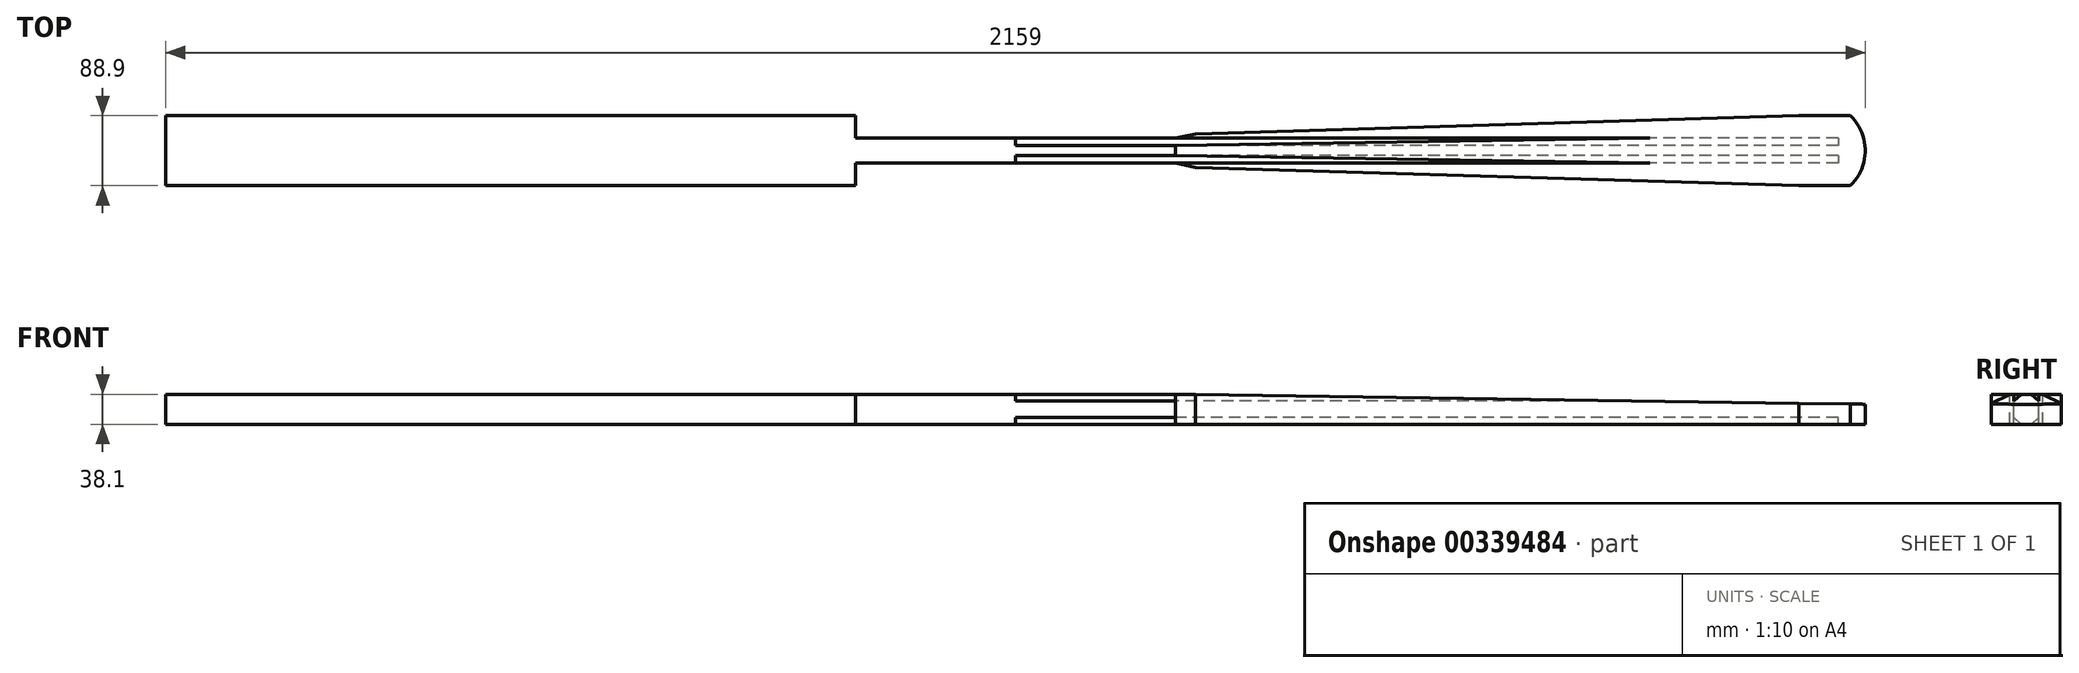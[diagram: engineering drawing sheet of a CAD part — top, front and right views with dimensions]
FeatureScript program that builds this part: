
annotation { "Feature Type Name" : "Feature", "Feature Type Description" : "" }
export const myFeature = defineFeature(function(context is Context, id is Id, definition is map)
    precondition{}
    {
        {
            assignVariable(context, id + "F0", {"name" : "L", "anyValue" : 85});
        }
        {
            assignVariable(context, id + "F1", {"name" : "S", "anyValue" : 16});
        }
        {
            var Q0;
            Q0=qCreatedBy(makeId("Top.planeOp"),FACE);
            var sketch = newSketch(context, id + "F2", { "sketchPlane" : qUnion([Q0])});
            skLineSegment(sketch, "E0.right", {"start": v(1079.5, 44.45) * mm, "end": v(1079.5, -44.45) * mm});
            skLineSegment(sketch, "E1.top", {"start": v(1079.5, -44.45) * mm, "end": v(-1079.5, -44.45) * mm});
            skLineSegment(sketch, "E1.right", {"start": v(-1079.5, 44.45) * mm, "end": v(-1079.5, -44.45) * mm});
            skLineSegment(sketch, "E2", {"start": v(-1079.5, 44.45) * mm, "end": v(1079.5, 44.45) * mm});
            skPoint(sketch, "E0.bottom.start.orphan", {"position": v(0, 0) * mm});
            skSolve(sketch);
        }
        {
            var Q0;
            Q0 = qSketchRegion(id + "F2", true);
            extrude(context, id + "F3", {"entities" : qUnion([Q0]), "depth" : 19.05 * mm, "hasSecondDirection" : true, "secondDirectionOppositeDirection" : true, "secondDirectionDepth" : 19.05 * mm});
        }
        {
            var Q0;
            Q0=makeQuery(id+"F3.opExtrude","CAP_FACE",FACE,{"disambiguationData":[OSD([sQuery(id+"F2.wireOp",EDGE,"E0.bottom"),sQuery(id+"F2.wireOp",EDGE,"E0.right"),sQuery(id+"F2.wireOp",EDGE,"E1.bottom"),sQuery(id+"F2.wireOp",EDGE,"E1.top"),sQuery(id+"F2.wireOp",EDGE,"E1.right")])],"isStart":false});
            var sketch = newSketch(context, id + "F4", { "sketchPlane" : qUnion([Q0])});
            skLineSegment(sketch, "E3.bottom", {"start": v(-203.2, 44.45) * mm, "end": v(203.2, 44.45) * mm});
            skLineSegment(sketch, "E3.top", {"start": v(-203.2, 15.88) * mm, "end": v(203.2, 15.88) * mm});
            skLineSegment(sketch, "E3.left", {"start": v(-203.2, 44.45) * mm, "end": v(-203.2, 15.88) * mm});
            skLineSegment(sketch, "E3.right", {"start": v(203.2, 44.45) * mm, "end": v(203.2, 15.88) * mm});
            skLineSegment(sketch, "E4.bottom", {"start": v(-203.2, -44.45) * mm, "end": v(203.2, -44.45) * mm});
            skLineSegment(sketch, "E4.top", {"start": v(-203.2, -15.87) * mm, "end": v(203.2, -15.87) * mm});
            skLineSegment(sketch, "E4.left", {"start": v(-203.2, -44.45) * mm, "end": v(-203.2, -15.87) * mm});
            skLineSegment(sketch, "E4.right", {"start": v(203.2, -44.45) * mm, "end": v(203.2, -15.87) * mm});
            skSolve(sketch);
        }
        {
            var Q0;
            Q0 = qSketchRegion(id + "F4", true);
            extrude(context, id + "F5", {"entities" : qUnion([Q0]), "operationType" : NewBodyOperationType.REMOVE, "endBound" : BoundingType.THROUGH_ALL, "oppositeDirection" : true, "depth" : 25.4 * mm});
        }
        {
            var Q0;
            Q0=qCreatedBy(makeId("Front.planeOp"),FACE);
            var sketch = newSketch(context, id + "F6", { "sketchPlane" : qUnion([Q0])});
            skPoint(sketch, "E5", {"position": v(203.2, 19.05) * mm});
            skPoint(sketch, "E6", {"position": v(203.2, -19.05) * mm});
            skLineSegment(sketch, "E7.0", {"start": v(1079.5, 19.05) * mm, "end": v(1079.5, 6.35) * mm});
            skLineSegment(sketch, "E8", {"start": v(203.2, 19.05) * mm, "end": v(1079.5, 6.35) * mm});
            skPoint(sketch, "E9.orphan", {"position": v(1079.5, 19.05) * mm});
            skLineSegment(sketch, "E10", {"start": v(1079.5, 19.05) * mm, "end": v(203.2, 19.05) * mm});
            skSolve(sketch);
        }
        {
            var Q0;
            Q0=qCreatedBy(makeId("Top.planeOp"),FACE);
            var sketch = newSketch(context, id + "F7", { "sketchPlane" : qUnion([Q0])});
            skLineSegment(sketch, "E11", {"start": v(995.05, 44.45) * mm, "end": v(228.6, 21.11) * mm});
            skLineSegment(sketch, "E12", {"start": v(228.6, 21.11) * mm, "end": v(203.2, 15.88) * mm});
            skLineSegment(sketch, "E13", {"start": v(203.2, 15.88) * mm, "end": v(203.2, 44.45) * mm});
            skLineSegment(sketch, "E14", {"start": v(203.2, 44.45) * mm, "end": v(995.05, 44.45) * mm});
            skLineSegment(sketch, "E15", {"start": v(995.05, -44.45) * mm, "end": v(228.6, -21.11) * mm});
            skLineSegment(sketch, "E16", {"start": v(203.2, -44.45) * mm, "end": v(995.05, -44.45) * mm});
            skLineSegment(sketch, "E17", {"start": v(228.6, -21.11) * mm, "end": v(203.2, -15.88) * mm});
            skLineSegment(sketch, "E18", {"start": v(203.2, -15.87) * mm, "end": v(203.2, -44.45) * mm});
            skSolve(sketch);
        }
        {
            var Q0;
            Q0 = qSketchRegion(id + "F6", true);
            extrude(context, id + "F8", {"entities" : qUnion([Q0]), "operationType" : NewBodyOperationType.REMOVE, "endBound" : BoundingType.THROUGH_ALL, "oppositeDirection" : true, "depth" : 25.4 * mm, "hasSecondDirection" : true, "secondDirectionBound" : SecondDirectionBoundingType.THROUGH_ALL, "secondDirectionOppositeDirection" : false, "secondDirectionDepth" : 25.4 * mm});
        }
        {
            var Q0;
            Q0 = qSketchRegion(id + "F7", true);
            extrude(context, id + "F9", {"entities" : qUnion([Q0]), "operationType" : NewBodyOperationType.REMOVE, "endBound" : BoundingType.THROUGH_ALL, "oppositeDirection" : true, "depth" : 25.4 * mm, "hasSecondDirection" : true, "secondDirectionBound" : SecondDirectionBoundingType.THROUGH_ALL, "secondDirectionOppositeDirection" : false, "secondDirectionDepth" : 25.4 * mm});
        }
        {
            var Q0;
            Q0=qCreatedBy(makeId("Top.planeOp"),FACE);
            var sketch = newSketch(context, id + "F10", { "sketchPlane" : qUnion([Q0])});
            skPoint(sketch, "E19", {"position": v(1079.5, 0) * mm});
            skPoint(sketch, "E20", {"position": v(1060.45, 44.45) * mm});
            skPoint(sketch, "E21", {"position": v(1060.45, -44.45) * mm});
            skArc(sketch, "E22", {"start": v(1060.45, -44.45) * mm, "mid": v(1079.5, 0) * mm, "end": v(1060.45, 44.45) * mm});
            skLineSegment(sketch, "E23.0", {"start": v(1079.5, 44.45) * mm, "end": v(1060.45, 44.45) * mm});
            skLineSegment(sketch, "E24.0", {"start": v(1060.45, -44.45) * mm, "end": v(1079.5, -44.45) * mm});
            skLineSegment(sketch, "E25.0", {"start": v(1079.5, 44.45) * mm, "end": v(1079.5, -44.45) * mm});
            skPoint(sketch, "E26.orphan", {"position": v(995.05, 44.45) * mm});
            skPoint(sketch, "E27.orphan", {"position": v(995.05, -44.45) * mm});
            skSolve(sketch);
        }
        {
            var Q0;
            Q0 = qSketchRegion(id + "F10", true);
            extrude(context, id + "F11", {"entities" : qUnion([Q0]), "operationType" : NewBodyOperationType.REMOVE, "endBound" : BoundingType.THROUGH_ALL, "oppositeDirection" : true, "depth" : 25.4 * mm, "hasSecondDirection" : true, "secondDirectionBound" : SecondDirectionBoundingType.THROUGH_ALL, "secondDirectionOppositeDirection" : false, "secondDirectionDepth" : 25.4 * mm});
        }
        {
            var Q0;
            {var subQ0=sQuery(id+"F10.wireOp",EDGE,"E22");Q0=makeQuery(id+"F11.boolean.opBoolean","INTERSECT",EDGE,{"derivedFrom":[makeQuery(id+"F8.boolean.opBoolean","COPY",FACE,{"derivedFrom":makeQuery(id+"F8.opExtrude","SWEPT_FACE",FACE,{"disambiguationData":[OSD([sQuery(id+"F6.wireOp",EDGE,"E8")])]})}),makeQuery(id+"F11.opExtrude","SWEPT_FACE",FACE,{"disambiguationData":[OSD([subQ0]),TDD([makeQuery(id+"F10.imprint","IMPRINT",EDGE,{"disambiguationData":[TD([[makeQuery(id+"F10.imprint","INTERSECT",VERTEX,{"derivedFrom":[subQ0,sQuery(id+"F10.wireOp",EDGE,"E24.0")]}),-1.0]])],"derivedFrom":subQ0})])]}),makeQuery(id+"F11.opExtrude","SWEPT_FACE",FACE,{"disambiguationData":[OSD([subQ0]),TDD([makeQuery(id+"F10.imprint","IMPRINT",EDGE,{"disambiguationData":[TD([[makeQuery(id+"F10.imprint","INTERSECT",VERTEX,{"derivedFrom":[subQ0,sQuery(id+"F10.wireOp",EDGE,"E23.0")]}),1.0]])],"derivedFrom":subQ0})])]})]});}
            cPoint(context, id + "F12", {"entities" : qUnion([Q0]), "parameter" : 0.5});
        }
        {
            var Q0;
            Q0 = qCreatedBy(id + "F12" ,VERTEX);
            var Q1;
            Q1=qCreatedBy(makeId("Right.planeOp"),FACE);
            cPlane(context, id + "F13", {"entities" : qUnion([Q0, Q1]), "cplaneType" : CPlaneType.PLANE_POINT, "offset" : 25.4 * mm, "width" : 152.4 * mm, "height" : 152.4 * mm});
        }
        {
            var Q0;
            Q0=qCreatedBy(id+"F13.planeOp",FACE);
            cPlane(context, id + "F14", {"entities" : qUnion([Q0]), "cplaneType" : CPlaneType.OFFSET, "offset" : (getVariable(context, 'L') / 2 - getVariable(context, 'S') / 2) * mm, "oppositeDirection" : true, "width" : 152.4 * mm, "height" : 152.4 * mm});
        }
        {
            var Q0;
            Q0=qCreatedBy(makeId("Right.planeOp"),FACE);
            var sketch = newSketch(context, id + "F15", { "sketchPlane" : qUnion([Q0])});
            skLineSegment(sketch, "E28.0", {"start": v(-15.87, -19.05) * mm, "end": v(-15.87, -10.32) * mm});
            skLineSegment(sketch, "E29.0", {"start": v(15.88, -19.05) * mm, "end": v(15.88, -10.32) * mm});
            skLineSegment(sketch, "E30.0", {"start": v(15.87, 19.05) * mm, "end": v(6.35, 19.05) * mm});
            skLineSegment(sketch, "E31.0", {"start": v(-6.35, -19.05) * mm, "end": v(-15.87, -19.05) * mm});
            skLineSegment(sketch, "E32", {"start": v(6.35, 19.05) * mm, "end": v(15.88, 10.32) * mm});
            skLineSegment(sketch, "E33", {"start": v(15.87, -10.32) * mm, "end": v(6.35, -19.05) * mm});
            skLineSegment(sketch, "E34", {"start": v(-6.35, -19.05) * mm, "end": v(-15.87, -10.32) * mm});
            skLineSegment(sketch, "E35", {"start": v(-15.88, 10.32) * mm, "end": v(-6.35, 19.05) * mm});
            skPoint(sketch, "E36.orphan", {"position": v(-15.88, 19.05) * mm});
            skPoint(sketch, "E37.orphan", {"position": v(15.88, 19.05) * mm});
            skPoint(sketch, "E38.orphan", {"position": v(15.87, -19.05) * mm});
            skPoint(sketch, "E39.orphan", {"position": v(-15.88, -19.05) * mm});
            skPoint(sketch, "E40.orphan", {"position": v(15.88, 10.32) * mm});
            skPoint(sketch, "E41.orphan", {"position": v(6.35, 19.05) * mm});
            skPoint(sketch, "E42.orphan", {"position": v(-15.88, 10.32) * mm});
            skPoint(sketch, "E43.orphan", {"position": v(-6.35, 19.05) * mm});
            skPoint(sketch, "E44.orphan", {"position": v(-15.88, -10.32) * mm});
            skPoint(sketch, "E45.orphan", {"position": v(6.35, -19.05) * mm});
            skPoint(sketch, "E46.orphan", {"position": v(-6.35, -19.05) * mm});
            skPoint(sketch, "E47.orphan", {"position": v(15.88, -10.32) * mm});
            skLineSegment(sketch, "E48.trimOffspring", {"start": v(15.88, 10.32) * mm, "end": v(15.88, 19.05) * mm});
            skLineSegment(sketch, "E49.trimOffspring", {"start": v(-6.35, 19.05) * mm, "end": v(-15.87, 19.05) * mm});
            skLineSegment(sketch, "E50.trimOffspring", {"start": v(15.87, -19.05) * mm, "end": v(6.35, -19.05) * mm});
            skLineSegment(sketch, "E51.trimOffspring", {"start": v(-15.88, 10.32) * mm, "end": v(-15.88, 19.05) * mm});
            skPoint(sketch, "E52.center.orphan", {"position": v(0, 7.43) * mm});
            skSolve(sketch);
        }
        {
            var Q0;
            Q0 = qSketchRegion(id + "F15", true);
            var Q1;
            Q1=qCreatedBy(id+"F14.planeOp",FACE);
            extrude(context, id + "F16", {"entities" : qUnion([Q0]), "operationType" : NewBodyOperationType.REMOVE, "endBound" : BoundingType.UP_TO_SURFACE, "endBoundEntityFace" : qUnion([Q1]), "depth" : 25.4 * mm});
        }
    });
